# Revit family: MR_ОсветительныйПрибор_Liniled
name_source: partatom
category: Осветительные приборы
units: mm (PartAtom-declared; Revit-internal decimal feet)

## family parameters
Всегда вертикально = Нет
Источник света = Да
На основе рабочей плоскости = Да
Общий = Да
При загрузке вырезать с полостями = Нет
Размер круглого соединителя = Использовать диаметр
Тип детали = Нормальный
Точка расчета площади = Нет

## types (4) — shared parameters
ADSK_URL страницы изделия = https://martinirus.ru
ADSK_Группирование = Наружное освещение_светильник
ADSK_Единица измерения = шт.
ADSK_Завод-изготовитель = MartiniRUS
ADSK_Классификация нагрузок = Освещение
ADSK_Количество = 1
ADSK_Количество фаз = 1
ADSK_Количество фаз числовое = 1
ADSK_Коэффициент мощности = 0.98
ADSK_Материал = <По категории>
ADSK_Напряжение = 24 В
ADSK_Ток = 0 А
IP Class = IP67
Видимая форма излучения при визуализации = Да
Группа модели = Liniled
Излучение по длине прямоугольника = 12 мм
Класс Защиты = III
Описание = Liniled
Отметка по умолчанию = 1219 мм
Самосветящий материал = Источник света по умолчанию
Светофильтр = 16777215
Смещение цветовой температуры при затухании лампы = <Нет>
Угол наклона = 90.00°
zero-valued in all types: ADSK_Масса

## per-type parameters (varying)
| type | ADSK_Код изделия | ADSK_Номинальная мощность | ADSK_Полная мощность | ADSK_Размер_Длина | Излучение по ширине прямоугольника | Полная установленная мощность | Файл фотометрической сетки |
| Liniled_Side_1000mm_3000k | P65696000WW(1000mm) | 11 Вт | 11 В·А | 1000 мм | 1000 мм | 11 В·А | P65696000WW_1000mm.ies |
| Liniled_Side_500mm_3000k | P65696000WW(500mm) | 5 Вт | 5 В·А | 500 мм | 500 мм | 5 В·А | P65696000WW_500mm.ies |
| Liniled_Side_100mm_3000k | P65696000WW(100mm) | 1 Вт | 1 В·А | 100 мм | 100 мм | 1 В·А | P65696000WW_100mm.ies |
| Liniled_Side_50mm_3000k | P65696000WW(50mm) | 1 Вт | 1 В·А | 50 мм | 50 мм | 1 В·А | P65696000WW_50mm.ies |

note: column(s) folded — value = type name in every type: ADSK_Наименование
